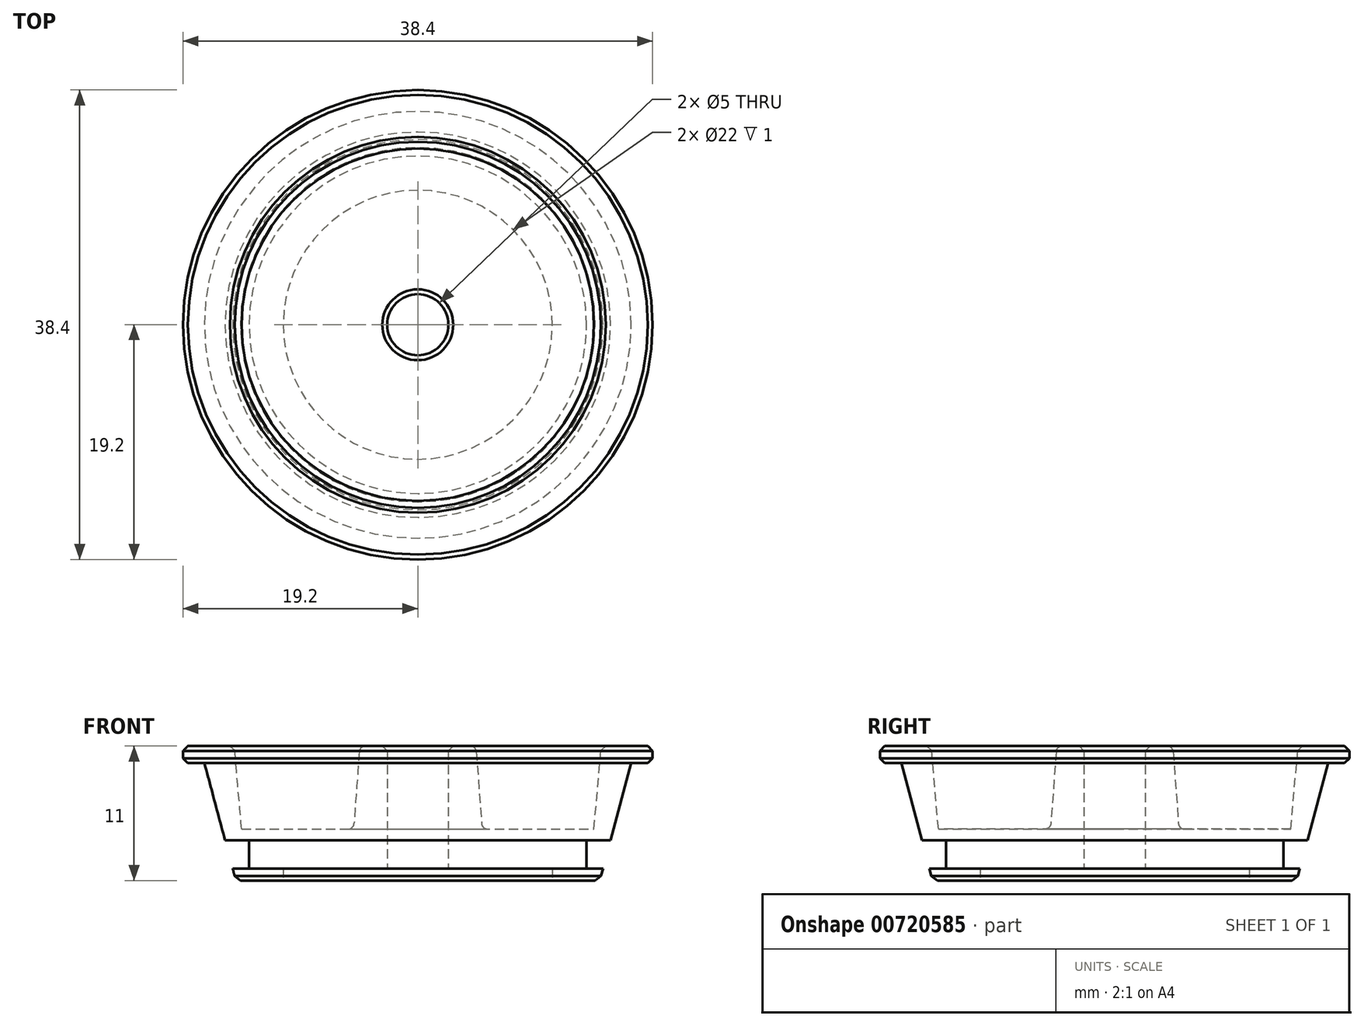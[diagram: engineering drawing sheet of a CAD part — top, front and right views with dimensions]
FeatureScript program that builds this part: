
annotation { "Feature Type Name" : "Feature", "Feature Type Description" : "" }
export const myFeature = defineFeature(function(context is Context, id is Id, definition is map)
    precondition{}
    {
        {
            var Q0;
            Q0=qCreatedBy(makeId("Front.planeOp"),FACE);
            var sketch = newSketch(context, id + "F0", { "sketchPlane" : qUnion([Q0])});
            skLineSegment(sketch, "E0", {"start": v(0, 0) * mm, "end": v(0, 11) * mm, "construction": true});
            skLineSegment(sketch, "E1", {"start": v(2.5, 11) * mm, "end": v(4.75, 11) * mm});
            skLineSegment(sketch, "E2", {"start": v(4.75, 11) * mm, "end": v(5.25, 4.2) * mm});
            skLineSegment(sketch, "E3", {"start": v(5.25, 4.2) * mm, "end": v(14.4, 4.2) * mm});
            skLineSegment(sketch, "E4", {"start": v(14.4, 4.2) * mm, "end": v(15, 11) * mm});
            skLineSegment(sketch, "E5", {"start": v(15, 11) * mm, "end": v(19.2, 11) * mm});
            skLineSegment(sketch, "E6", {"start": v(19.2, 11) * mm, "end": v(19.2, 9.6) * mm});
            skLineSegment(sketch, "E7", {"start": v(19.2, 9.6) * mm, "end": v(17.45, 9.6) * mm});
            skLineSegment(sketch, "E8", {"start": v(17.45, 9.6) * mm, "end": v(15.76, 3.29) * mm});
            skLineSegment(sketch, "E9", {"start": v(15.76, 3.29) * mm, "end": v(13.8, 3.29) * mm});
            skLineSegment(sketch, "E10", {"start": v(13.8, 3.29) * mm, "end": v(13.8, 0.99) * mm});
            skLineSegment(sketch, "E11", {"start": v(13.8, 0.99) * mm, "end": v(15.14, 0.99) * mm});
            skLineSegment(sketch, "E12", {"start": v(15.14, 0.99) * mm, "end": v(14.88, 0) * mm});
            skLineSegment(sketch, "E13", {"start": v(14.88, 0) * mm, "end": v(2.5, 0) * mm});
            skLineSegment(sketch, "E14", {"start": v(2.5, 11) * mm, "end": v(2.5, 0) * mm});
            skLineSegment(sketch, "E15", {"start": v(15.76, 3.29) * mm, "end": v(15.14, 0.99) * mm, "construction": true});
            skPoint(sketch, "E16", {"position": v(15.45, 2.14) * mm});
            skCircle(sketch, "E17", {"center": v(14.7, 2.4) * mm, "radius": 0.89 * mm, "construction": true});
            skSolve(sketch);
        }
        {
            var Q0;
            Q0=makeQuery(id+"F0.imprint","IMPRINT",FACE,{"disambiguationData":[TD([[makeQuery(id+"F0.imprint","IMPRINT",EDGE,{"derivedFrom":sQuery(id+"F0.wireOp",EDGE,"E1")}),-1.0]])]});
            var Q1;
            Q1=sQuery(id+"F0.wireOp",EDGE,"E0");
            revolve(context, id + "F1", {"surfaceOperationType" : NewSurfaceOperationType.NEW, "entities" : qUnion([Q0]), "axis" : qUnion([Q1]), "revolveType" : RevolveType.FULL});
        }
        {
            var Q0;
            Q0=makeQuery(id+"F1.opRevolve","SWEPT_EDGE",EDGE,{"disambiguationData":[OSD([sQuery(id+"F0.wireOp",EDGE,"E1"),sQuery(id+"F0.wireOp",EDGE,"E14")])]});
            var Q1;
            Q1=makeQuery(id+"F1.opRevolve","SWEPT_FACE",FACE,{"disambiguationData":[OSD([sQuery(id+"F0.wireOp",EDGE,"E5")])]});
            var Q2;
            Q2=makeQuery(id+"F1.opRevolve","SWEPT_EDGE",EDGE,{"disambiguationData":[OSD([sQuery(id+"F0.wireOp",EDGE,"E6"),sQuery(id+"F0.wireOp",EDGE,"E7")])]});
            chamfer(context, id + "F2", {"entities" : qUnion([Q0, Q1, Q2]), "width" : 0.4 * mm, "tangentPropagation" : true});
        }
        {
            var Q0;
            Q0=makeQuery(id+"F1.opRevolve","SWEPT_FACE",FACE,{"disambiguationData":[OSD([sQuery(id+"F0.wireOp",EDGE,"E2")])]});
            fillet(context, id + "F3", {"entities" : qUnion([Q0]), "radius" : 0.5 * mm, "tangentPropagation" : true, "allowEdgeOverflow" : false});
        }
        {
            var Q0;
            Q0=makeQuery(id+"F1.opRevolve","SWEPT_FACE",FACE,{"disambiguationData":[OSD([sQuery(id+"F0.wireOp",EDGE,"E13")])]});
            var sketch = newSketch(context, id + "F4", { "sketchPlane" : qUnion([Q0])});
            skCircle(sketch, "E18", {"center": v(0, 0) * mm, "radius": 11 * mm});
            skSolve(sketch);
        }
        {
            var Q0;
            Q0 = qSketchRegion(id + "F4", true);
            extrude(context, id + "F5", {"entities" : qUnion([Q0]), "operationType" : NewBodyOperationType.REMOVE, "oppositeDirection" : true, "depth" : 1 * mm, "offsetDistance" : 25 * mm});
        }
        {
            var Q0;
            Q0=makeQuery(id+"F1.opRevolve","SWEPT_EDGE",EDGE,{"disambiguationData":[OSD([sQuery(id+"F0.wireOp",EDGE,"E12"),sQuery(id+"F0.wireOp",EDGE,"E13")])]});
            chamfer(context, id + "F6", {"entities" : qUnion([Q0]), "width" : 0.5 * mm, "tangentPropagation" : true});
        }
    });
